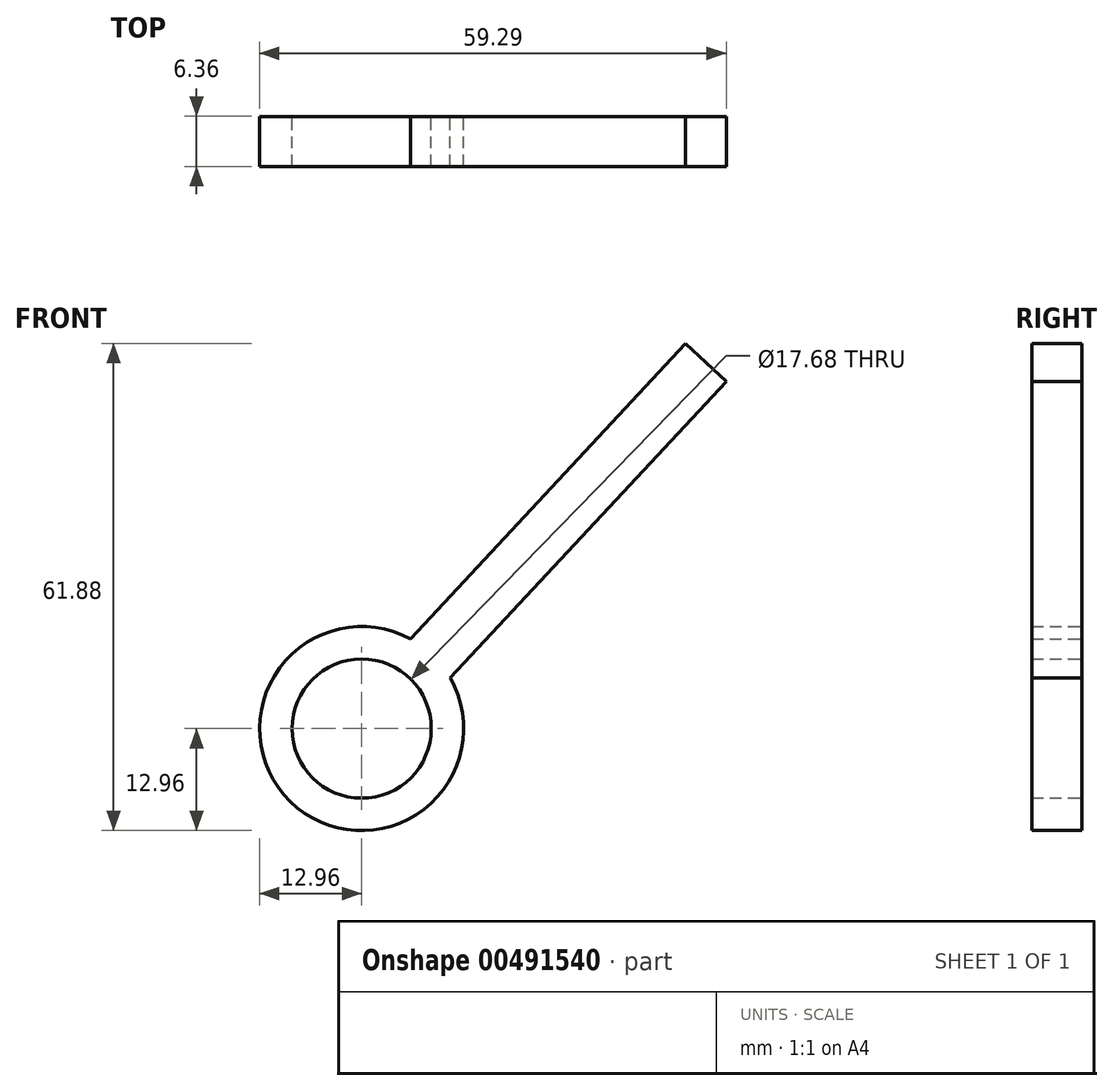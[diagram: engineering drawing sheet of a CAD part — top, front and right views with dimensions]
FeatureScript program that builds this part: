
annotation { "Feature Type Name" : "Feature", "Feature Type Description" : "" }
export const myFeature = defineFeature(function(context is Context, id is Id, definition is map)
    precondition{}
    {
        {
            var Q0;
            Q0=qCreatedBy(makeId("Front.planeOp"),FACE);
            var sketch = newSketch(context, id + "F0", { "sketchPlane" : qUnion([Q0])});
            skCircle(sketch, "E0", {"center": v(0, 0) * mm, "radius": 12.96 * mm});
            skCircle(sketch, "E1", {"center": v(0, 0) * mm, "radius": 8.84 * mm});
            skLineSegment(sketch, "E2", {"start": v(3.25, 8.22) * mm, "end": v(41.14, 48.92) * mm});
            skLineSegment(sketch, "E3", {"start": v(41.14, 48.92) * mm, "end": v(46.33, 44.09) * mm});
            skLineSegment(sketch, "E4", {"start": v(46.33, 44.09) * mm, "end": v(8.9, 3.88) * mm});
            skSolve(sketch);
        }
        {
            var Q0;
            {var subQ5=sQuery(id+"F0.wireOp",EDGE,"E3");Q0=makeQuery(id+"F0.imprint","IMPRINT",FACE,{"disambiguationData":[TD([[makeQuery(id+"F0.imprint","IMPRINT",EDGE,{"derivedFrom":subQ5}),-1.0]])]});}
            var Q1;
            Q1=makeQuery(id+"F0.imprint","IMPRINT",FACE,{"disambiguationData":[TD([[makeQuery(id+"F0.imprint","IMPRINT",EDGE,{"derivedFrom":sQuery(id+"F0.wireOp",EDGE,"E1")}),-1.0]])]});
            extrude(context, id + "F1", {"entities" : qUnion([Q0, Q1]), "endBound" : BoundingType.SYMMETRIC, "depth" : 6.35 * mm});
        }
    });
